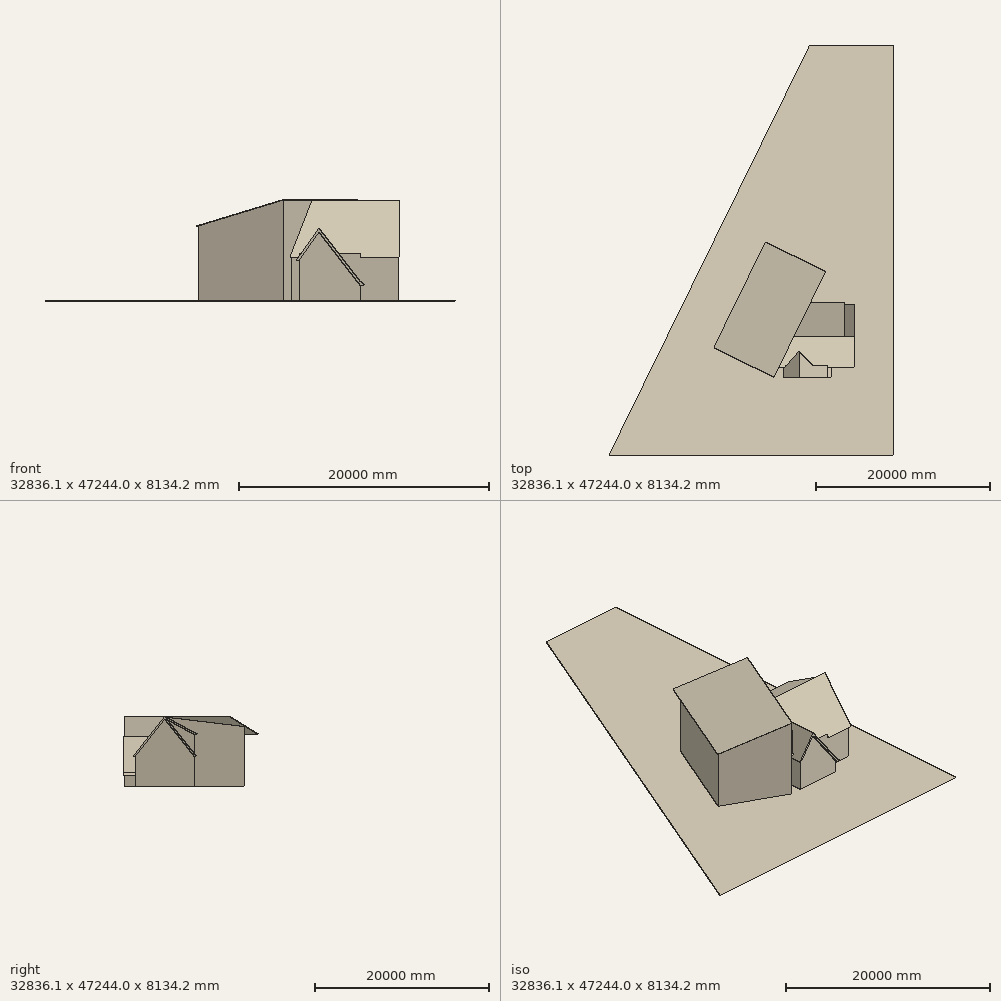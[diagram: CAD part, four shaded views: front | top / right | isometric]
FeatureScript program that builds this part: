
annotation { "Feature Type Name" : "Feature", "Feature Type Description" : "" }
export const myFeature = defineFeature(function(context is Context, id is Id, definition is map)
    precondition{}
    {
        {
            var Q0;
            Q0=qCreatedBy(makeId("Top.planeOp"),FACE);
            var sketch = newSketch(context, id + "F0", { "sketchPlane" : qUnion([Q0])});
            skLineSegment(sketch, "E0", {"start": v(0, 47244) * mm, "end": v(0, 0) * mm});
            skLineSegment(sketch, "E1", {"start": v(0, 0) * mm, "end": v(-32836.1, 0) * mm});
            skLineSegment(sketch, "E2", {"start": v(-32836.1, 0) * mm, "end": v(-9704.83, 47244) * mm});
            skLineSegment(sketch, "E3", {"start": v(-9704.83, 47244) * mm, "end": v(0, 47244) * mm});
            skSolve(sketch);
        }
        {
            var Q0;
            Q0=makeQuery(id+"F0.imprint","IMPRINT",FACE,{"disambiguationData":[TD([[makeQuery(id+"F0.imprint","IMPRINT",EDGE,{"derivedFrom":sQuery(id+"F0.wireOp",EDGE,"E0")}),-1.0]])]});
            extrude(context, id + "F1", {"entities" : qUnion([Q0]), "depth" : 25.4 * mm});
        }
        {
            var Q0;
            Q0=makeQuery(id+"F1.opExtrude","CAP_FACE",FACE,{"disambiguationData":[OSD([sQuery(id+"F0.wireOp",EDGE,"E0"),sQuery(id+"F0.wireOp",EDGE,"E1"),sQuery(id+"F0.wireOp",EDGE,"E2"),sQuery(id+"F0.wireOp",EDGE,"E3")])],"isStart":false});
            var sketch = newSketch(context, id + "F2", { "sketchPlane" : qUnion([Q0])});
            skLineSegment(sketch, "E4.bottom", {"start": v(-13197.84, 17160.24) * mm, "end": v(-4572, 17160.24) * mm});
            skLineSegment(sketch, "E4.top", {"start": v(-13197.84, 10363.2) * mm, "end": v(-4572, 10363.2) * mm});
            skLineSegment(sketch, "E4.left", {"start": v(-13197.84, 17160.24) * mm, "end": v(-13197.84, 10363.2) * mm});
            skLineSegment(sketch, "E4.right", {"start": v(-4572, 17160.24) * mm, "end": v(-4572, 10363.2) * mm});
            skLineSegment(sketch, "E5.bottom", {"start": v(-13045.44, 17007.84) * mm, "end": v(-4724.4, 17007.84) * mm});
            skLineSegment(sketch, "E5.top", {"start": v(-13045.44, 10515.6) * mm, "end": v(-4724.4, 10515.6) * mm});
            skLineSegment(sketch, "E5.left", {"start": v(-13045.44, 17007.84) * mm, "end": v(-13045.44, 10515.6) * mm});
            skLineSegment(sketch, "E5.right", {"start": v(-4724.4, 17007.84) * mm, "end": v(-4724.4, 10515.6) * mm});
            skSolve(sketch);
        }
        {
            var Q0;
            Q0=makeQuery(id+"F2.imprint","IMPRINT",FACE,{"disambiguationData":[TD([[makeQuery(id+"F2.imprint","IMPRINT",EDGE,{"derivedFrom":sQuery(id+"F2.wireOp",EDGE,"E4.bottom")}),-1.0]])]});
            extrude(context, id + "F3", {"entities" : qUnion([Q0]), "offsetDistance" : 30.48 * mm, "depth" : 7734 * mm});
        }
        {
            var Q0;
            Q0=makeQuery(id+"F1.opExtrude","CAP_FACE",FACE,{"disambiguationData":[OSD([sQuery(id+"F0.wireOp",EDGE,"E0"),sQuery(id+"F0.wireOp",EDGE,"E1"),sQuery(id+"F0.wireOp",EDGE,"E2"),sQuery(id+"F0.wireOp",EDGE,"E3")])],"isStart":false});
            var sketch = newSketch(context, id + "F4", { "sketchPlane" : qUnion([Q0])});
            skLineSegment(sketch, "E6", {"start": v(-13197.84, 17160.24) * mm, "end": v(-17465.04, 17160.24) * mm});
            skLineSegment(sketch, "E7", {"start": v(-17465.04, 17160.24) * mm, "end": v(-17465.04, 11064.24) * mm});
            skLineSegment(sketch, "E8", {"start": v(-17465.04, 11064.24) * mm, "end": v(-13197.84, 11064.24) * mm});
            skLineSegment(sketch, "E9", {"start": v(-13197.84, 17007.84) * mm, "end": v(-17312.64, 17007.84) * mm});
            skLineSegment(sketch, "E10", {"start": v(-17312.64, 17007.84) * mm, "end": v(-17312.64, 11216.64) * mm});
            skLineSegment(sketch, "E11", {"start": v(-17312.64, 11216.64) * mm, "end": v(-13197.84, 11216.64) * mm});
            skLineSegment(sketch, "E12", {"start": v(-13197.84, 17160.24) * mm, "end": v(-13197.84, 17007.84) * mm});
            skLineSegment(sketch, "E13", {"start": v(-10808.26, 7562.78) * mm, "end": v(-10586.18, 7562.78) * mm});
            skLineSegment(sketch, "E14", {"start": v(-13197.84, 11216.64) * mm, "end": v(-13197.84, 11064.24) * mm});
            skSolve(sketch);
        }
        {
            var Q0;
            Q0=makeQuery(id+"F4.imprint","IMPRINT",FACE,{"disambiguationData":[TD([[makeQuery(id+"F4.imprint","IMPRINT",EDGE,{"derivedFrom":sQuery(id+"F4.wireOp",EDGE,"E6")}),1.0]])]});
            extrude(context, id + "F5", {"entities" : qUnion([Q0]), "depth" : 3048 * mm});
        }
        {
            var Q0;
            Q0=makeQuery(id+"F1.opExtrude","CAP_FACE",FACE,{"disambiguationData":[OSD([sQuery(id+"F0.wireOp",EDGE,"E0"),sQuery(id+"F0.wireOp",EDGE,"E1"),sQuery(id+"F0.wireOp",EDGE,"E2"),sQuery(id+"F0.wireOp",EDGE,"E3")])],"isStart":false});
            var sketch = newSketch(context, id + "F6", { "sketchPlane" : qUnion([Q0])});
            skLineSegment(sketch, "E15", {"start": v(-12496.8, 10363.2) * mm, "end": v(-12496.8, 9144) * mm});
            skLineSegment(sketch, "E16", {"start": v(-12496.8, 9144) * mm, "end": v(-7620, 9144) * mm});
            skLineSegment(sketch, "E17", {"start": v(-7620, 9144) * mm, "end": v(-7620, 10363.2) * mm});
            skLineSegment(sketch, "E18", {"start": v(-7620, 10363.2) * mm, "end": v(-7772.4, 10363.2) * mm});
            skLineSegment(sketch, "E19", {"start": v(-7772.4, 10363.2) * mm, "end": v(-7772.4, 9296.4) * mm});
            skLineSegment(sketch, "E20", {"start": v(-7772.4, 9296.4) * mm, "end": v(-12344.4, 9296.4) * mm});
            skLineSegment(sketch, "E21", {"start": v(-12344.4, 9296.4) * mm, "end": v(-12344.4, 10363.2) * mm});
            skLineSegment(sketch, "E22", {"start": v(-12344.4, 10363.2) * mm, "end": v(-12496.8, 10363.2) * mm});
            skSolve(sketch);
        }
        {
            var Q0;
            Q0=makeQuery(id+"F6.imprint","IMPRINT",FACE,{"disambiguationData":[TD([[makeQuery(id+"F6.imprint","IMPRINT",EDGE,{"derivedFrom":sQuery(id+"F6.wireOp",EDGE,"E15")}),1.0]])]});
            extrude(context, id + "F7", {"entities" : qUnion([Q0]), "offsetDistance" : 30.48 * mm, "depth" : 5486.4 * mm});
        }
        {
            var Q0;
            Q0=makeQuery(id+"F3.opExtrude","SWEPT_FACE",FACE,{"disambiguationData":[OSD([sQuery(id+"F2.wireOp",EDGE,"E4.right")])]});
            var sketch = newSketch(context, id + "F8", { "sketchPlane" : qUnion([Q0])});
            skLineSegment(sketch, "E23", {"start": v(10363.2, 3479.79) * mm, "end": v(13761.72, 7759.4) * mm});
            skLineSegment(sketch, "E24", {"start": v(13761.72, 7759.4) * mm, "end": v(17160.24, 3479.79) * mm});
            skLineSegment(sketch, "E25", {"start": v(10363.2, 3479.79) * mm, "end": v(10363.2, 7759.4) * mm});
            skLineSegment(sketch, "E26", {"start": v(10363.2, 7759.4) * mm, "end": v(17160.24, 7759.4) * mm});
            skLineSegment(sketch, "E27", {"start": v(17160.24, 7759.4) * mm, "end": v(17160.24, 3479.79) * mm});
            skSolve(sketch);
        }
        {
            var Q0;
            {var subQ0=sQuery(id+"F8.wireOp",EDGE,"E24");Q0=makeQuery(id+"F8.imprint","IMPRINT",FACE,{"disambiguationData":[TD([[makeQuery(id+"F8.imprint","IMPRINT",EDGE,{"derivedFrom":subQ0}),1.0]])]});}
            var Q1;
            {var subQ0=sQuery(id+"F8.wireOp",EDGE,"E23");Q1=makeQuery(id+"F8.imprint","IMPRINT",FACE,{"disambiguationData":[TD([[makeQuery(id+"F8.imprint","IMPRINT",EDGE,{"derivedFrom":subQ0}),1.0]])]});}
            var Q2;
            Q2=makeQuery(id+"F3.opExtrude","SWEPT_FACE",FACE,{"disambiguationData":[OSD([sQuery(id+"F2.wireOp",EDGE,"E4.left")])]});
            extrude(context, id + "F9", {"entities" : qUnion([Q0, Q1]), "operationType" : NewBodyOperationType.REMOVE, "endBound" : BoundingType.UP_TO_SURFACE, "oppositeDirection" : true, "depth" : 30.48 * mm, "endBoundEntityFace" : qUnion([Q2]), "offsetDistance" : 30.48 * mm});
        }
        {
            var Q0;
            Q0=makeQuery(id+"F3.opExtrude","SWEPT_FACE",FACE,{"disambiguationData":[OSD([sQuery(id+"F2.wireOp",EDGE,"E4.right")])]});
            var sketch = newSketch(context, id + "F10", { "sketchPlane" : qUnion([Q0])});
            skLineSegment(sketch, "E28", {"start": v(10103.72, 3479.79) * mm, "end": v(13761.72, 8086.14) * mm});
            skLineSegment(sketch, "E29", {"start": v(13761.72, 8086.14) * mm, "end": v(17419.72, 3479.79) * mm});
            skLineSegment(sketch, "E30", {"start": v(17419.72, 3479.79) * mm, "end": v(17160.24, 3479.79) * mm});
            skLineSegment(sketch, "E31", {"start": v(17160.24, 3479.79) * mm, "end": v(13761.72, 7759.4) * mm});
            skLineSegment(sketch, "E32", {"start": v(13761.72, 7759.4) * mm, "end": v(10363.2, 3479.79) * mm});
            skLineSegment(sketch, "E33", {"start": v(10363.2, 3479.79) * mm, "end": v(10103.72, 3479.79) * mm});
            skSolve(sketch);
        }
        {
            var Q0;
            {var subQ6=sQuery(id+"F10.wireOp",EDGE,"E29");var subQ7=sQuery(id+"F10.wireOp",EDGE,"E28");var subQ8=makeQuery(id+"F10.imprint","INTERSECT",VERTEX,{"derivedFrom":[subQ7,subQ6]});Q0=makeQuery(id+"F10.imprint","IMPRINT",FACE,{"disambiguationData":[TD([[makeQuery(id+"F10.imprint","IMPRINT",EDGE,{"disambiguationData":[TD([[subQ8,1.0]])],"derivedFrom":subQ7}),-1.0]])]});}
            extrude(context, id + "F11", {"entities" : qUnion([Q0]), "operationType" : NewBodyOperationType.ADD, "depth" : 76.2 * mm, "offsetDistance" : 30.48 * mm, "hasSecondDirection" : true, "secondDirectionOppositeDirection" : true, "secondDirectionDepth" : 8702.04 * mm});
        }
        {
            var Q0;
            Q0=makeQuery(id+"F7.opExtrude","SWEPT_FACE",FACE,{"disambiguationData":[OSD([sQuery(id+"F6.wireOp",EDGE,"E16")])]});
            var sketch = newSketch(context, id + "F12", { "sketchPlane" : qUnion([Q0])});
            skLineSegment(sketch, "E34", {"start": v(-12496.8, 3276.6) * mm, "end": v(-10922.02, 5511.8) * mm});
            skLineSegment(sketch, "E35", {"start": v(-10922.02, 5511.8) * mm, "end": v(-7620, 1244.6) * mm});
            skLineSegment(sketch, "E36", {"start": v(-7620, 1244.6) * mm, "end": v(-7620, 5511.8) * mm});
            skLineSegment(sketch, "E37", {"start": v(-7620, 5511.8) * mm, "end": v(-12496.8, 5511.8) * mm});
            skLineSegment(sketch, "E38", {"start": v(-12496.8, 5511.8) * mm, "end": v(-12496.8, 3276.6) * mm});
            skSolve(sketch);
        }
        {
            var Q0;
            Q0=qSketchRegion(id+"F12",true);
            var Q1;
            Q1=makeQuery(id+"F7.opExtrude","SWEPT_FACE",FACE,{"disambiguationData":[OSD([sQuery(id+"F6.wireOp",EDGE,"E22")])]});
            var Q2;
            Q2=makeQuery(id+"F3.opExtrude","SWEPT_BODY",BODY,{"disambiguationData":[OSD([sQuery(id+"F2.wireOp",EDGE,"E4.bottom"),sQuery(id+"F2.wireOp",EDGE,"E4.top"),sQuery(id+"F2.wireOp",EDGE,"E4.left"),sQuery(id+"F2.wireOp",EDGE,"E4.right"),sQuery(id+"F2.wireOp",EDGE,"E5.bottom"),sQuery(id+"F2.wireOp",EDGE,"E5.top"),sQuery(id+"F2.wireOp",EDGE,"E5.left"),sQuery(id+"F2.wireOp",EDGE,"E5.right")])]});
            extrude(context, id + "F13", {"entities" : qUnion([Q0]), "operationType" : NewBodyOperationType.REMOVE, "endBound" : BoundingType.UP_TO_SURFACE, "oppositeDirection" : true, "depth" : 30.48 * mm, "endBoundEntityFace" : qUnion([Q1]), "endBoundEntityBody" : qUnion([Q2]), "offsetDistance" : 30.48 * mm});
        }
        {
            var Q0;
            Q0=makeQuery(id+"F7.opExtrude","SWEPT_FACE",FACE,{"disambiguationData":[OSD([sQuery(id+"F6.wireOp",EDGE,"E16")])]});
            var sketch = newSketch(context, id + "F14", { "sketchPlane" : qUnion([Q0])});
            skLineSegment(sketch, "E39", {"start": v(-10922.02, 5511.8) * mm, "end": v(-12496.8, 3276.6) * mm});
            skLineSegment(sketch, "E40", {"start": v(-12496.8, 3276.6) * mm, "end": v(-12730.73, 3276.6) * mm});
            skLineSegment(sketch, "E41", {"start": v(-12730.73, 3276.6) * mm, "end": v(-10922.02, 5843.83) * mm});
            skLineSegment(sketch, "E42", {"start": v(-10922.02, 5843.83) * mm, "end": v(-7670.8, 1642.28) * mm});
            skLineSegment(sketch, "E43", {"start": v(-7670.8, 1642.28) * mm, "end": v(-7213.6, 1244.6) * mm});
            skLineSegment(sketch, "E44", {"start": v(-7213.6, 1244.6) * mm, "end": v(-7620, 1244.6) * mm});
            skLineSegment(sketch, "E45", {"start": v(-7620, 1244.6) * mm, "end": v(-10922.02, 5511.8) * mm});
            skSolve(sketch);
        }
        {
            var Q0;
            Q0=makeQuery(id+"F14.imprint","IMPRINT",FACE,{"disambiguationData":[TD([[makeQuery(id+"F14.imprint","IMPRINT",EDGE,{"derivedFrom":sQuery(id+"F14.wireOp",EDGE,"E39")}),1.0]])]});
            var Q1;
            Q1=makeQuery(id+"F3.opExtrude","SWEPT_BODY",BODY,{"disambiguationData":[OSD([sQuery(id+"F2.wireOp",EDGE,"E4.bottom"),sQuery(id+"F2.wireOp",EDGE,"E4.top"),sQuery(id+"F2.wireOp",EDGE,"E4.left"),sQuery(id+"F2.wireOp",EDGE,"E4.right"),sQuery(id+"F2.wireOp",EDGE,"E5.bottom"),sQuery(id+"F2.wireOp",EDGE,"E5.top"),sQuery(id+"F2.wireOp",EDGE,"E5.left"),sQuery(id+"F2.wireOp",EDGE,"E5.right")])]});
            var Q2;
            Q2=makeQuery(id+"F3.opExtrude","SWEPT_BODY",BODY,{"disambiguationData":[OSD([sQuery(id+"F2.wireOp",EDGE,"E4.bottom"),sQuery(id+"F2.wireOp",EDGE,"E4.top"),sQuery(id+"F2.wireOp",EDGE,"E4.left"),sQuery(id+"F2.wireOp",EDGE,"E4.right"),sQuery(id+"F2.wireOp",EDGE,"E5.bottom"),sQuery(id+"F2.wireOp",EDGE,"E5.top"),sQuery(id+"F2.wireOp",EDGE,"E5.left"),sQuery(id+"F2.wireOp",EDGE,"E5.right")])]});
            extrude(context, id + "F15", {"entities" : qUnion([Q0]), "depth" : 152.4 * mm, "endBoundEntityBody" : qUnion([Q1]), "offsetDistance" : 30.48 * mm, "hasSecondDirection" : true, "secondDirectionBound" : SecondDirectionBoundingType.UP_TO_BODY, "secondDirectionOppositeDirection" : true, "secondDirectionDepth" : 152.4 * mm, "secondDirectionBoundEntityBody" : qUnion([Q2])});
        }
        {
            var Q0;
            Q0=qCreatedBy(makeId("Top.planeOp"),FACE);
            cPlane(context, id + "F16", {"entities" : qUnion([Q0]), "cplaneType" : CPlaneType.OFFSET, "offset" : 12192 * mm, "width" : 152.4 * mm, "height" : 152.4 * mm});
        }
        {
            var Q0;
            Q0=qCreatedBy(id+"F16.planeOp",FACE);
            var sketch = newSketch(context, id + "F17", { "sketchPlane" : qUnion([Q0])});
            skLineSegment(sketch, "E46", {"start": v(-11978.64, 17160.24) * mm, "end": v(-5791.2, 17160.24) * mm});
            skLineSegment(sketch, "E47", {"start": v(-5791.2, 17160.24) * mm, "end": v(-5791.2, 13761.72) * mm});
            skLineSegment(sketch, "E48", {"start": v(-5791.2, 13761.72) * mm, "end": v(-6019.8, 13761.72) * mm});
            skLineSegment(sketch, "E49", {"start": v(-6019.8, 13761.72) * mm, "end": v(-6019.8, 17007.84) * mm});
            skLineSegment(sketch, "E50", {"start": v(-6019.8, 17007.84) * mm, "end": v(-11750.04, 17007.84) * mm});
            skLineSegment(sketch, "E51", {"start": v(-11750.04, 17007.84) * mm, "end": v(-11750.04, 13761.72) * mm});
            skLineSegment(sketch, "E52", {"start": v(-11750.04, 13761.72) * mm, "end": v(-11978.64, 13761.72) * mm});
            skLineSegment(sketch, "E53", {"start": v(-11978.64, 13761.72) * mm, "end": v(-11978.64, 17160.24) * mm});
            skSolve(sketch);
        }
        {
            var Q0;
            Q0=makeQuery(id+"F17.imprint","IMPRINT",FACE,{"disambiguationData":[TD([[makeQuery(id+"F17.imprint","IMPRINT",EDGE,{"derivedFrom":sQuery(id+"F17.wireOp",EDGE,"E46")}),-1.0]])]});
            var Q1;
            Q1=makeQuery(id+"F3.opExtrude","SWEPT_BODY",BODY,{"disambiguationData":[OSD([sQuery(id+"F2.wireOp",EDGE,"E4.bottom"),sQuery(id+"F2.wireOp",EDGE,"E4.top"),sQuery(id+"F2.wireOp",EDGE,"E4.left"),sQuery(id+"F2.wireOp",EDGE,"E4.right"),sQuery(id+"F2.wireOp",EDGE,"E5.bottom"),sQuery(id+"F2.wireOp",EDGE,"E5.top"),sQuery(id+"F2.wireOp",EDGE,"E5.left"),sQuery(id+"F2.wireOp",EDGE,"E5.right")])]});
            extrude(context, id + "F18", {"entities" : qUnion([Q0]), "operationType" : NewBodyOperationType.ADD, "endBound" : BoundingType.UP_TO_BODY, "oppositeDirection" : true, "depth" : 30.48 * mm, "endBoundEntityBody" : qUnion([Q1]), "offsetDistance" : 30.48 * mm});
        }
        {
            var Q0;
            Q0=makeQuery(id+"F18.opExtrude","SWEPT_FACE",FACE,{"disambiguationData":[OSD([sQuery(id+"F17.wireOp",EDGE,"E47")])]});
            var sketch = newSketch(context, id + "F19", { "sketchPlane" : qUnion([Q0])});
            skLineSegment(sketch, "E54", {"start": v(13761.72, 8086.14) * mm, "end": v(17160.24, 6019.8) * mm});
            skLineSegment(sketch, "E55", {"start": v(17160.24, 6019.8) * mm, "end": v(17160.24, 12192) * mm});
            skLineSegment(sketch, "E56", {"start": v(17160.24, 12192) * mm, "end": v(13761.72, 12192) * mm});
            skLineSegment(sketch, "E57", {"start": v(13761.72, 12192) * mm, "end": v(13761.72, 8086.14) * mm});
            skSolve(sketch);
        }
        {
            var Q0;
            {var subQ5=sQuery(id+"F19.wireOp",EDGE,"E55");Q0=makeQuery(id+"F19.imprint","IMPRINT",FACE,{"disambiguationData":[TD([[makeQuery(id+"F19.imprint","IMPRINT",EDGE,{"derivedFrom":subQ5}),1.0]])]});}
            var Q1;
            Q1=makeQuery(id+"F18.opExtrude","SWEPT_FACE",FACE,{"disambiguationData":[OSD([sQuery(id+"F17.wireOp",EDGE,"E53")])]});
            extrude(context, id + "F20", {"entities" : qUnion([Q0]), "operationType" : NewBodyOperationType.REMOVE, "endBound" : BoundingType.UP_TO_SURFACE, "oppositeDirection" : true, "depth" : 30.48 * mm, "endBoundEntityFace" : qUnion([Q1]), "offsetDistance" : 30.48 * mm});
        }
        {
            var Q0;
            Q0=makeQuery(id+"F18.opExtrude","SWEPT_FACE",FACE,{"disambiguationData":[OSD([sQuery(id+"F17.wireOp",EDGE,"E47")])]});
            var sketch = newSketch(context, id + "F21", { "sketchPlane" : qUnion([Q0])});
            skLineSegment(sketch, "E58", {"start": v(13761.72, 7855.2) * mm, "end": v(17160.24, 6019.8) * mm});
            skLineSegment(sketch, "E59", {"start": v(17160.24, 6019.8) * mm, "end": v(17587.86, 6019.8) * mm});
            skLineSegment(sketch, "E60", {"start": v(17587.86, 6019.8) * mm, "end": v(13761.72, 8086.14) * mm});
            skLineSegment(sketch, "E61", {"start": v(13761.72, 8086.14) * mm, "end": v(13761.72, 7855.2) * mm});
            skSolve(sketch);
        }
        {
            var Q0;
            Q0=qSketchRegion(id+"F21",true);
            extrude(context, id + "F22", {"entities" : qUnion([Q0]), "operationType" : NewBodyOperationType.ADD, "depth" : 76.2 * mm, "offsetDistance" : 30.48 * mm, "hasSecondDirection" : true, "secondDirectionOppositeDirection" : true, "secondDirectionDepth" : 6263.64 * mm});
        }
        {
            var Q0;
            Q0=makeQuery(id+"F18.opExtrude","SWEPT_FACE",FACE,{"disambiguationData":[OSD([sQuery(id+"F17.wireOp",EDGE,"E47")])]});
            var sketch = newSketch(context, id + "F23", { "sketchPlane" : qUnion([Q0])});
            skLineSegment(sketch, "E62", {"start": v(17160.24, 3479.79) * mm, "end": v(17160.24, 3806.54) * mm});
            skLineSegment(sketch, "E63", {"start": v(17160.24, 3806.54) * mm, "end": v(17419.72, 3479.79) * mm});
            skLineSegment(sketch, "E64", {"start": v(17419.72, 3479.79) * mm, "end": v(17160.24, 3479.79) * mm});
            skSolve(sketch);
        }
        {
            var Q0;
            Q0=makeQuery(id+"F23.imprint","IMPRINT",FACE,{"disambiguationData":[TD([[makeQuery(id+"F23.imprint","IMPRINT",EDGE,{"derivedFrom":sQuery(id+"F23.wireOp",EDGE,"E62")}),-1.0]])]});
            var Q1;
            Q1=makeQuery(id+"F18.opExtrude","SWEPT_FACE",FACE,{"disambiguationData":[OSD([sQuery(id+"F17.wireOp",EDGE,"E53")])]});
            extrude(context, id + "F24", {"entities" : qUnion([Q0]), "operationType" : NewBodyOperationType.REMOVE, "endBound" : BoundingType.UP_TO_SURFACE, "oppositeDirection" : true, "depth" : 3048 * mm, "endBoundEntityFace" : qUnion([Q1]), "offsetDistance" : 30.48 * mm});
        }
        {
            var Q0;
            Q0=makeQuery(id+"F1.opExtrude","CAP_FACE",FACE,{"disambiguationData":[OSD([sQuery(id+"F0.wireOp",EDGE,"E0"),sQuery(id+"F0.wireOp",EDGE,"E1"),sQuery(id+"F0.wireOp",EDGE,"E2"),sQuery(id+"F0.wireOp",EDGE,"E3")])],"isStart":false});
            var sketch = newSketch(context, id + "F25", { "sketchPlane" : qUnion([Q0])});
            skLineSegment(sketch, "E65", {"start": v(-11483.04, 13761.72) * mm, "end": v(-13743.93, 9144) * mm});
            skLineSegment(sketch, "E66", {"start": v(-13743.93, 9144) * mm, "end": v(-20587.66, 12494.78) * mm});
            skLineSegment(sketch, "E67", {"start": v(-20587.66, 12494.78) * mm, "end": v(-15494.48, 22897.25) * mm});
            skLineSegment(sketch, "E68", {"start": v(-15494.48, 22897.25) * mm, "end": v(-11750.04, 22897.25) * mm});
            skLineSegment(sketch, "E69", {"start": v(-11750.04, 22897.25) * mm, "end": v(-11750.04, 13761.72) * mm});
            skLineSegment(sketch, "E70", {"start": v(-11978.64, 13761.72) * mm, "end": v(-11978.64, 22668.65) * mm});
            skLineSegment(sketch, "E71", {"start": v(-11978.64, 22668.65) * mm, "end": v(-15351.88, 22668.65) * mm});
            skLineSegment(sketch, "E72", {"start": v(-15351.88, 22668.65) * mm, "end": v(-20281.83, 12599.57) * mm});
            skLineSegment(sketch, "E73", {"start": v(-20281.83, 12599.57) * mm, "end": v(-13848.72, 9449.84) * mm});
            skLineSegment(sketch, "E74", {"start": v(-13848.72, 9449.84) * mm, "end": v(-11737.57, 13761.72) * mm});
            skLineSegment(sketch, "E75", {"start": v(-11978.64, 13761.72) * mm, "end": v(-11750.04, 13761.72) * mm});
            skLineSegment(sketch, "E76", {"start": v(-11737.57, 13761.72) * mm, "end": v(-11483.04, 13761.72) * mm});
            skSolve(sketch);
        }
        {
            var Q0;
            Q0=makeQuery(id+"F25.imprint","IMPRINT",FACE,{"disambiguationData":[TD([[makeQuery(id+"F25.imprint","IMPRINT",EDGE,{"derivedFrom":sQuery(id+"F25.wireOp",EDGE,"E65")}),-1.0]])]});
            extrude(context, id + "F26", {"entities" : qUnion([Q0]), "depth" : 10363.2 * mm, "offsetDistance" : 30.48 * mm});
        }
        {
            var Q0;
            Q0=makeQuery(id+"F26.opExtrude","SWEPT_FACE",FACE,{"disambiguationData":[OSD([sQuery(id+"F25.wireOp",EDGE,"E66")])]});
            var sketch = newSketch(context, id + "F27", { "sketchPlane" : qUnion([Q0])});
            skLineSegment(sketch, "E77", {"start": v(-16364.74, 10388.6) * mm, "end": v(-23984.74, 10388.6) * mm});
            skLineSegment(sketch, "E78", {"start": v(-23984.74, 10388.6) * mm, "end": v(-23984.74, 6019.78) * mm});
            skLineSegment(sketch, "E79", {"start": v(-23984.74, 6019.78) * mm, "end": v(-16364.74, 8102.6) * mm});
            skLineSegment(sketch, "E80", {"start": v(-16364.74, 8102.6) * mm, "end": v(-16364.74, 10388.6) * mm});
            skSolve(sketch);
        }
        {
            var Q0;
            Q0=makeQuery(id+"F27.imprint","IMPRINT",FACE,{"disambiguationData":[TD([[makeQuery(id+"F27.imprint","IMPRINT",EDGE,{"derivedFrom":sQuery(id+"F27.wireOp",EDGE,"E77")}),1.0]])]});
            var Q1;
            Q1=makeQuery(id+"F26.opExtrude","SWEPT_FACE",FACE,{"disambiguationData":[OSD([sQuery(id+"F25.wireOp",EDGE,"E68")])]});
            extrude(context, id + "F28", {"entities" : qUnion([Q0]), "operationType" : NewBodyOperationType.REMOVE, "endBound" : BoundingType.UP_TO_SURFACE, "oppositeDirection" : true, "depth" : 30.48 * mm, "endBoundEntityFace" : qUnion([Q1]), "offsetDistance" : 30.48 * mm});
        }
        {
            var Q0;
            Q0=makeQuery(id+"F26.opExtrude","SWEPT_FACE",FACE,{"disambiguationData":[OSD([sQuery(id+"F25.wireOp",EDGE,"E66")])]});
            var sketch = newSketch(context, id + "F29", { "sketchPlane" : qUnion([Q0])});
            skLineSegment(sketch, "E81", {"start": v(-16364.74, 8102.6) * mm, "end": v(-16364.74, 8134.2) * mm});
            skLineSegment(sketch, "E82", {"start": v(-16364.74, 8134.2) * mm, "end": v(-24100.34, 6019.78) * mm});
            skLineSegment(sketch, "E83", {"start": v(-24100.34, 6019.78) * mm, "end": v(-23984.74, 6019.78) * mm});
            skLineSegment(sketch, "E84", {"start": v(-23984.74, 6019.78) * mm, "end": v(-16364.74, 8102.6) * mm});
            skSolve(sketch);
        }
        {
            var Q0;
            Q0=makeQuery(id+"F29.imprint","IMPRINT",FACE,{"disambiguationData":[TD([[makeQuery(id+"F29.imprint","IMPRINT",EDGE,{"derivedFrom":sQuery(id+"F29.wireOp",EDGE,"E81")}),1.0]])]});
            extrude(context, id + "F30", {"entities" : qUnion([Q0]), "depth" : 152.4 * mm, "offsetDistance" : 30.48 * mm, "hasSecondDirection" : true, "secondDirectionOppositeDirection" : true, "secondDirectionDepth" : 13411.2 * mm});
        }
    });
